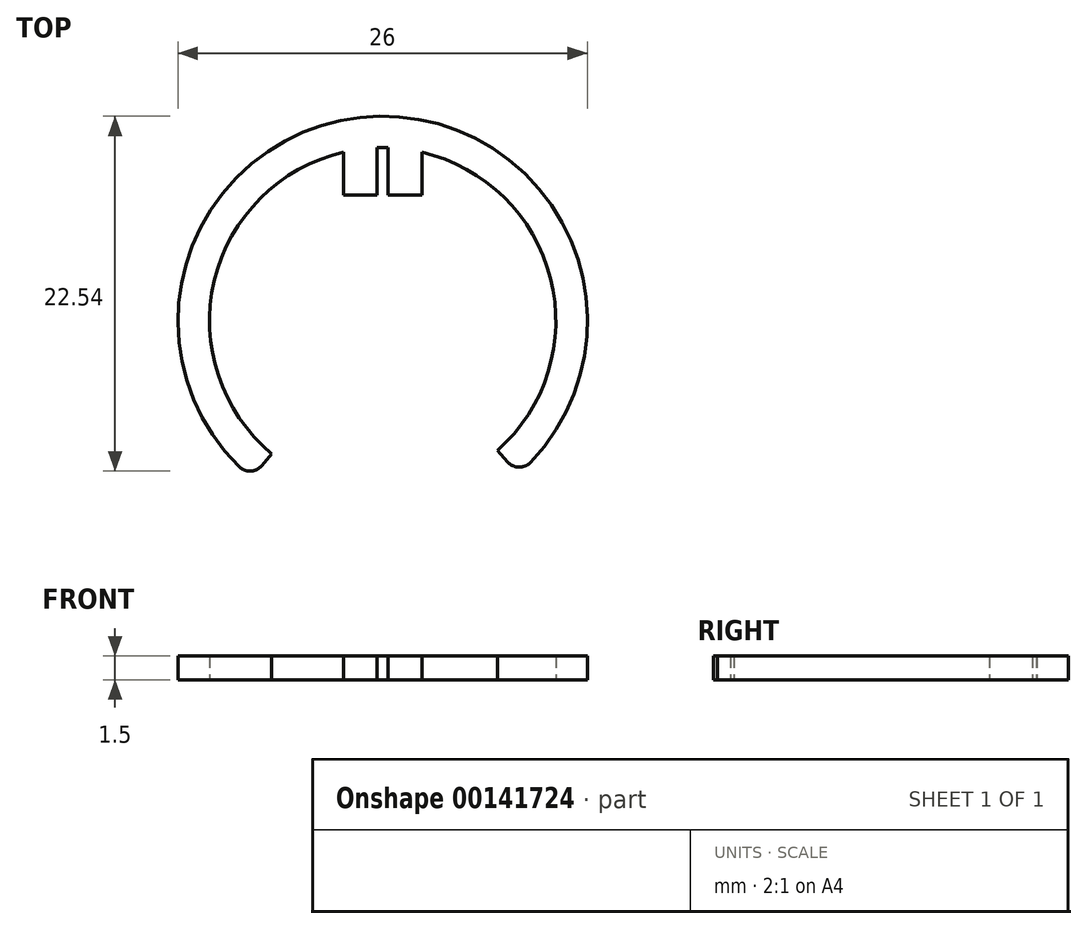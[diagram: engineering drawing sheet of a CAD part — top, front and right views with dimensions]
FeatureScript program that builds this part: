
annotation { "Feature Type Name" : "Feature", "Feature Type Description" : "" }
export const myFeature = defineFeature(function(context is Context, id is Id, definition is map)
    precondition{}
    {
        {
            var Q0;
            Q0=qCreatedBy(makeId("Top.planeOp"),FACE);
            var Q1;
            Q1=qCreatedBy(makeId("Top.planeOp"),FACE);
            var sketch = newSketch(context, id + "F0", { "sketchPlane" : qUnion([Q0, Q1])});
            skCircle(sketch, "E0", {"center": v(0, 0) * mm, "radius": 11 * mm});
            skCircle(sketch, "E1", {"center": v(0, 0) * mm, "radius": 13 * mm});
            skLineSegment(sketch, "E2", {"start": v(0, 0) * mm, "end": v(-8.33, -9.98) * mm});
            skLineSegment(sketch, "E3", {"start": v(0, 0) * mm, "end": v(8.62, -9.73) * mm});
            skLineSegment(sketch, "E4", {"start": v(-2.5, 10.71) * mm, "end": v(-2.5, 8) * mm});
            skLineSegment(sketch, "E5", {"start": v(-2.5, 8) * mm, "end": v(2.5, 8) * mm});
            skLineSegment(sketch, "E6", {"start": v(2.5, 8) * mm, "end": v(2.5, 10.71) * mm});
            skLineSegment(sketch, "E7", {"start": v(-0.35, 8) * mm, "end": v(-0.35, 11) * mm});
            skLineSegment(sketch, "E8", {"start": v(0.35, 8) * mm, "end": v(0.35, 11) * mm});
            skSolve(sketch);
        }
        {
            var Q0;
            {var subQ0=sQuery(id+"F0.wireOp",EDGE,"E0");var subQ8=makeQuery(id+"F0.imprint","INTERSECT",VERTEX,{"derivedFrom":[subQ0,sQuery(id+"F0.wireOp",EDGE,"E6")]});Q0=makeQuery(id+"F0.imprint","IMPRINT",FACE,{"disambiguationData":[TD([[makeQuery(id+"F0.imprint","IMPRINT",EDGE,{"disambiguationData":[TD([[subQ8,-1.0]])],"derivedFrom":subQ0}),-1.0]])]});}
            var Q1;
            {var subQ0=sQuery(id+"F0.wireOp",EDGE,"E4");Q1=makeQuery(id+"F0.imprint","IMPRINT",FACE,{"disambiguationData":[TD([[makeQuery(id+"F0.imprint","IMPRINT",EDGE,{"derivedFrom":subQ0}),1.0]])]});}
            var Q2;
            {var subQ0=sQuery(id+"F0.wireOp",EDGE,"E6");Q2=makeQuery(id+"F0.imprint","IMPRINT",FACE,{"disambiguationData":[TD([[makeQuery(id+"F0.imprint","IMPRINT",EDGE,{"derivedFrom":subQ0}),1.0]])]});}
            extrude(context, id + "F1", {"entities" : qUnion([Q0, Q1, Q2]), "depth" : 1.5 * mm});
        }
        {
            var Q0;
            Q0=makeQuery(id+"F1.opExtrude","SWEPT_EDGE",EDGE,{"disambiguationData":[OSD([sQuery(id+"F0.wireOp",EDGE,"E1"),sQuery(id+"F0.wireOp",EDGE,"E2")])]});
            var Q1;
            Q1=makeQuery(id+"F1.opExtrude","SWEPT_EDGE",EDGE,{"disambiguationData":[OSD([sQuery(id+"F0.wireOp",EDGE,"E1"),sQuery(id+"F0.wireOp",EDGE,"E3")])]});
            fillet(context, id + "F2", {"entities" : qUnion([Q0, Q1]), "radius" : 1 * mm, "tangentPropagation" : true, "allowEdgeOverflow" : false});
        }
    });
